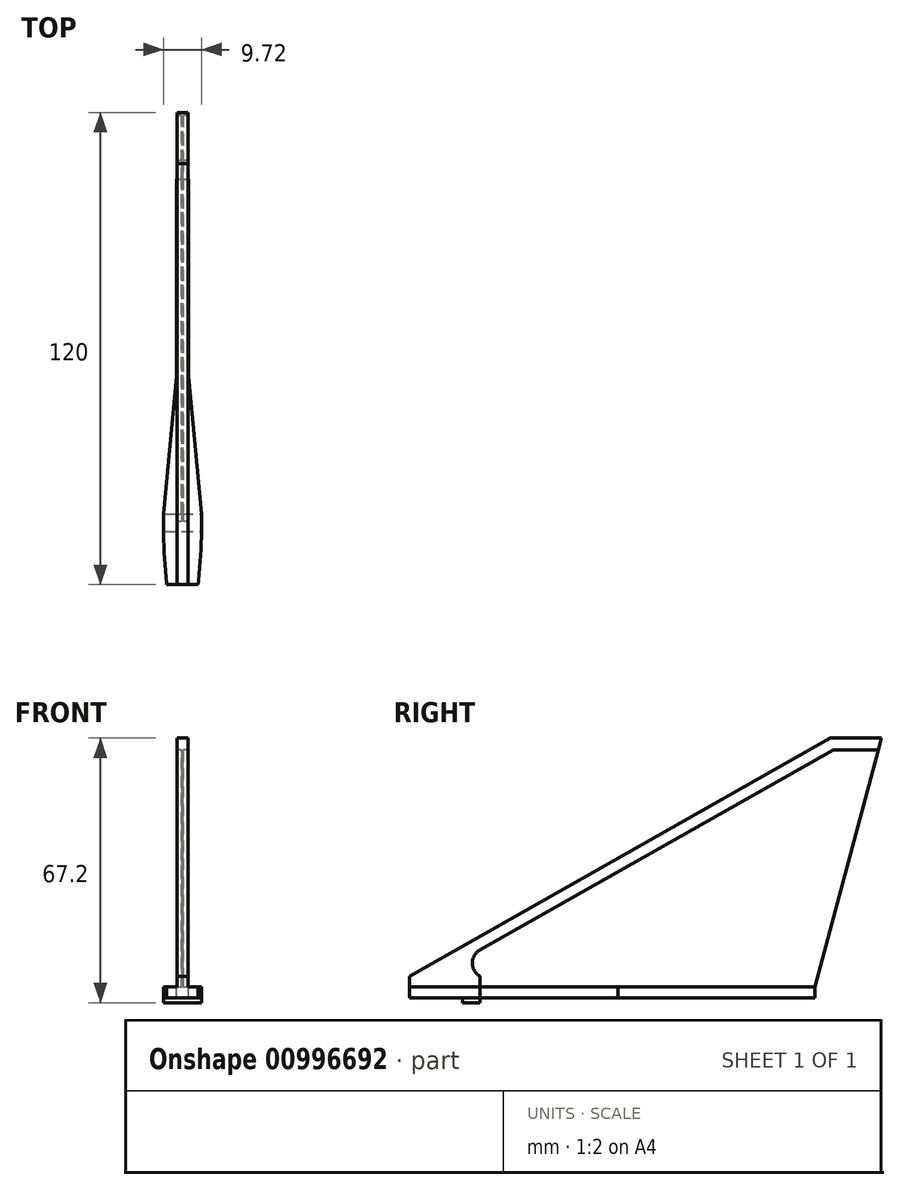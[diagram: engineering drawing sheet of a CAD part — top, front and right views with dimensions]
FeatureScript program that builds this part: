
annotation { "Feature Type Name" : "Feature", "Feature Type Description" : "" }
export const myFeature = defineFeature(function(context is Context, id is Id, definition is map)
    precondition{}
    {
        {
            var Q0;
            Q0=qCreatedBy(makeId("Front.planeOp"),FACE);
            var sketch = newSketch(context, id + "F0", { "sketchPlane" : qUnion([Q0])});
            skLineSegment(sketch, "E0.bottom", {"start": v(-4, 0) * mm, "end": v(4, 0) * mm});
            skLineSegment(sketch, "E0.top", {"start": v(-4, 2.8) * mm, "end": v(-1.4, 2.8) * mm});
            skLineSegment(sketch, "E0.left", {"start": v(-4, 0) * mm, "end": v(-4, 2.8) * mm});
            skLineSegment(sketch, "E0.right", {"start": v(4, 0) * mm, "end": v(4, 2.8) * mm});
            skLineSegment(sketch, "E1.top", {"start": v(-1.4, 5.5) * mm, "end": v(1.4, 5.5) * mm});
            skLineSegment(sketch, "E1.left", {"start": v(-1.4, 2.8) * mm, "end": v(-1.4, 5.5) * mm});
            skLineSegment(sketch, "E1.right", {"start": v(1.4, 2.8) * mm, "end": v(1.4, 5.5) * mm});
            skLineSegment(sketch, "E2", {"start": v(0, -1.58) * mm, "end": v(0, 6.32) * mm, "construction": true});
            skLineSegment(sketch, "E3.trimOffspring", {"start": v(1.4, 2.8) * mm, "end": v(4, 2.8) * mm});
            skSolve(sketch);
        }
        {
            var Q0;
            Q0=qCreatedBy(makeId("Front.planeOp"),FACE);
            cPlane(context, id + "F1", {"entities" : qUnion([Q0]), "cplaneType" : CPlaneType.OFFSET, "offset" : 13.5 * mm, "oppositeDirection" : true, "width" : 150 * mm, "height" : 150 * mm});
        }
        {
            var Q0;
            Q0=qCreatedBy(id+"F1.planeOp",FACE);
            var sketch = newSketch(context, id + "F2", { "sketchPlane" : qUnion([Q0])});
            skLineSegment(sketch, "E4.bottom", {"start": v(-4.85, 0) * mm, "end": v(4.85, 0) * mm});
            skLineSegment(sketch, "E4.top", {"start": v(-4.85, 2.8) * mm, "end": v(-1.4, 2.8) * mm});
            skLineSegment(sketch, "E4.left", {"start": v(-4.85, 0) * mm, "end": v(-4.85, 2.8) * mm});
            skLineSegment(sketch, "E4.right", {"start": v(4.85, 0) * mm, "end": v(4.85, 2.8) * mm});
            skLineSegment(sketch, "E5.top", {"start": v(-1.4, 5.5) * mm, "end": v(1.4, 5.5) * mm});
            skLineSegment(sketch, "E5.left", {"start": v(-1.4, 2.8) * mm, "end": v(-1.4, 5.5) * mm});
            skLineSegment(sketch, "E5.right", {"start": v(1.4, 2.8) * mm, "end": v(1.4, 5.5) * mm});
            skLineSegment(sketch, "E6", {"start": v(0, -4.65) * mm, "end": v(0, 9.3) * mm, "construction": true});
            skLineSegment(sketch, "E7.trimOffspring", {"start": v(1.4, 2.8) * mm, "end": v(4.85, 2.8) * mm});
            skPoint(sketch, "E8.0", {"position": v(0, 0) * mm});
            skSolve(sketch);
        }
        {
            var Q0;
            Q0=qCreatedBy(id+"F1.planeOp",FACE);
            cPlane(context, id + "F3", {"entities" : qUnion([Q0]), "cplaneType" : CPlaneType.OFFSET, "offset" : 4.5 * mm, "oppositeDirection" : true, "width" : 150 * mm, "height" : 150 * mm});
        }
        {
            var Q0;
            Q0=qCreatedBy(id+"F3.planeOp",FACE);
            var sketch = newSketch(context, id + "F4", { "sketchPlane" : qUnion([Q0])});
            skLineSegment(sketch, "E9.0", {"start": v(-1.4, 2.8) * mm, "end": v(-1.4, 5.5) * mm});
            skLineSegment(sketch, "E9.1", {"start": v(-1.4, 5.5) * mm, "end": v(1.4, 5.5) * mm});
            skLineSegment(sketch, "E9.2", {"start": v(4.85, 0) * mm, "end": v(4.85, 2.8) * mm});
            skLineSegment(sketch, "E9.3", {"start": v(-4.85, 0) * mm, "end": v(-4.85, 2.8) * mm});
            skLineSegment(sketch, "E9.4", {"start": v(1.4, 2.8) * mm, "end": v(4.85, 2.8) * mm});
            skLineSegment(sketch, "E9.5", {"start": v(0, -4.65) * mm, "end": v(0, 9.3) * mm, "construction": true});
            skLineSegment(sketch, "E9.6", {"start": v(-4.85, 2.8) * mm, "end": v(-1.4, 2.8) * mm});
            skLineSegment(sketch, "E9.7", {"start": v(-4.85, 0) * mm, "end": v(4.85, 0) * mm});
            skLineSegment(sketch, "E9.8", {"start": v(1.4, 2.8) * mm, "end": v(1.4, 5.5) * mm});
            skSolve(sketch);
        }
        {
            var Q0;
            Q0=qCreatedBy(id+"F3.planeOp",FACE);
            var sketch = newSketch(context, id + "F5", { "sketchPlane" : qUnion([Q0])});
            skLineSegment(sketch, "E10.0", {"start": v(-4.85, 0) * mm, "end": v(-4.85, 2.8) * mm});
            skLineSegment(sketch, "E11.0", {"start": v(-4.85, 0) * mm, "end": v(4.85, 0) * mm});
            skLineSegment(sketch, "E12.0", {"start": v(4.85, 0) * mm, "end": v(4.85, 2.8) * mm});
            skLineSegment(sketch, "E13.0", {"start": v(0, -4.65) * mm, "end": v(0, 9.3) * mm, "construction": true});
            skLineSegment(sketch, "E14", {"start": v(-4.85, 2.8) * mm, "end": v(4.85, 2.8) * mm});
            skSolve(sketch);
        }
        {
            var Q0;
            Q0=qCreatedBy(id+"F3.planeOp",FACE);
            cPlane(context, id + "F6", {"entities" : qUnion([Q0]), "cplaneType" : CPlaneType.OFFSET, "offset" : 35 * mm, "oppositeDirection" : true, "width" : 150 * mm, "height" : 150 * mm});
        }
        {
            var Q0;
            Q0=qCreatedBy(id+"F6.planeOp",FACE);
            var sketch = newSketch(context, id + "F7", { "sketchPlane" : qUnion([Q0])});
            skPoint(sketch, "E15.0", {"position": v(0, 0) * mm});
            skLineSegment(sketch, "E16.bottom", {"start": v(-1.5, 0) * mm, "end": v(1.5, 0) * mm});
            skLineSegment(sketch, "E16.left", {"start": v(-1.5, 0) * mm, "end": v(-1.5, 2.8) * mm});
            skLineSegment(sketch, "E16.right", {"start": v(1.5, 0) * mm, "end": v(1.5, 2.8) * mm});
            skLineSegment(sketch, "E17", {"start": v(0, -1.58) * mm, "end": v(0, 6.32) * mm, "construction": true});
            skLineSegment(sketch, "E18", {"start": v(-1.5, 2.8) * mm, "end": v(1.5, 2.8) * mm});
            skSolve(sketch);
        }
        {
            var Q0;
            Q0=makeQuery(id+"F0.imprint","IMPRINT",FACE,{"disambiguationData":[TD([[makeQuery(id+"F0.imprint","IMPRINT",EDGE,{"derivedFrom":sQuery(id+"F0.wireOp",EDGE,"E0.bottom")}),1.0]])]});
            var Q1;
            Q1=makeQuery(id+"F2.imprint","IMPRINT",FACE,{"disambiguationData":[TD([[makeQuery(id+"F2.imprint","IMPRINT",EDGE,{"derivedFrom":sQuery(id+"F2.wireOp",EDGE,"E4.bottom")}),1.0]])]});
            var Q2;
            Q2=makeQuery(id+"F4.imprint","IMPRINT",FACE,{"disambiguationData":[TD([[makeQuery(id+"F4.imprint","IMPRINT",EDGE,{"derivedFrom":sQuery(id+"F4.wireOp",EDGE,"E9.0")}),-1.0]])]});
            loft(context, id + "F8", {"sheetProfilesArray" : [{ "sheetProfileEntities" : qUnion([Q0]) }, { "sheetProfileEntities" : qUnion([Q1]) }, { "sheetProfileEntities" : qUnion([Q2]) }]});
        }
        {
            var Q1;
            Q1 = qSketchRegion(id + "F5", true);
            var Q2;
            Q2 = qSketchRegion(id + "F7", true);
            loft(context, id + "F9", {"operationType" : NewBodyOperationType.ADD, "sheetProfilesArray" : [{ "sheetProfileEntities" : qUnion([Q1]) }, { "sheetProfileEntities" : qUnion([Q2]) }]});
        }
        {
            var Q0;
            Q0 = qSketchRegion(id + "F7", true);
            extrude(context, id + "F10", {"entities" : qUnion([Q0]), "operationType" : NewBodyOperationType.ADD, "oppositeDirection" : true, "depth" : 50 * mm, "offsetDistance" : 25 * mm});
        }
        {
            var Q0;
            {var subQ0=sQuery(id+"F7.wireOp",EDGE,"E16.bottom");Q0=makeQuery(id+"F10.boolean.opBoolean","MERGE",FACE,{"derivedFrom":[makeQuery(id+"F9.boolean.opBoolean","MERGE",FACE,{"derivedFrom":[makeQuery(id+"F8.opLoft","SWEPT_FACE",FACE,{"disambiguationData":[OSD([sQuery(id+"F0.wireOp",EDGE,"E0.bottom"),sQuery(id+"F0.wireOp",EDGE,"E0.left"),sQuery(id+"F0.wireOp",EDGE,"E0.right"),sQuery(id+"F2.wireOp",EDGE,"E4.bottom"),sQuery(id+"F2.wireOp",EDGE,"E4.left"),sQuery(id+"F2.wireOp",EDGE,"E4.right"),sQuery(id+"F4.wireOp",EDGE,"E9.2"),sQuery(id+"F4.wireOp",EDGE,"E9.3"),sQuery(id+"F4.wireOp",EDGE,"E9.7")])]}),makeQuery(id+"F9.opLoft","SWEPT_FACE",FACE,{"disambiguationData":[OSD([sQuery(id+"F5.wireOp",EDGE,"E10.0"),sQuery(id+"F5.wireOp",EDGE,"E11.0"),sQuery(id+"F5.wireOp",EDGE,"E12.0"),subQ0,sQuery(id+"F7.wireOp",EDGE,"E16.left"),sQuery(id+"F7.wireOp",EDGE,"E16.right")])]})]}),makeQuery(id+"F10.opExtrude","SWEPT_FACE",FACE,{"disambiguationData":[OSD([subQ0])]})]});}
            var sketch = newSketch(context, id + "F11", { "sketchPlane" : qUnion([Q0])});
            skFitSpline(sketch, "E19.0", {"points": [v(-4, 0) * mm, v(-4.39, -4.5) * mm, v(-4.9, -10.5) * mm, v(-4.86, -16.5) * mm, v(-4.85, -18) * mm], "construction": true});
            skFitSpline(sketch, "E20.0", {"points": [v(4, 0) * mm, v(4.39, -4.5) * mm, v(4.9, -10.5) * mm, v(4.86, -16.5) * mm, v(4.85, -18) * mm], "construction": true});
            skPoint(sketch, "E21.0", {"position": v(-4.85, -18) * mm});
            skLineSegment(sketch, "E22", {"start": v(-4.85, -13.5) * mm, "end": v(4.85, -13.5) * mm});
            skLineSegment(sketch, "E23", {"start": v(-4.85, -18) * mm, "end": v(4.85, -18) * mm});
            skLineSegment(sketch, "E24", {"start": v(-4.85, -13.5) * mm, "end": v(-4.85, -18) * mm});
            skLineSegment(sketch, "E25", {"start": v(4.85, -18) * mm, "end": v(4.85, -13.5) * mm});
            skSolve(sketch);
        }
        {
            var Q0;
            Q0 = qSketchRegion(id + "F11", true);
            extrude(context, id + "F12", {"entities" : qUnion([Q0]), "operationType" : NewBodyOperationType.ADD, "depth" : 1.2 * mm, "offsetDistance" : 25 * mm});
        }
        {
            var Q0;
            Q0=qCreatedBy(makeId("Right.planeOp"),FACE);
            var sketch = newSketch(context, id + "F13", { "sketchPlane" : qUnion([Q0])});
            skLineSegment(sketch, "E26", {"start": v(103, 2.8) * mm, "end": v(18, 2.8) * mm, "construction": true});
            skLineSegment(sketch, "E27", {"start": v(103, 2.8) * mm, "end": v(103, 0) * mm, "construction": true});
            skLineSegment(sketch, "E28", {"start": v(18, 0) * mm, "end": v(103, 0) * mm, "construction": true});
            skLineSegment(sketch, "E29", {"start": v(0, 0) * mm, "end": v(13.5, 0) * mm, "construction": true});
            skLineSegment(sketch, "E30", {"start": v(0, 5.5) * mm, "end": v(0, 0) * mm, "construction": true});
            skLineSegment(sketch, "E31", {"start": v(18, 5.5) * mm, "end": v(0, 5.5) * mm, "construction": true});
            skLineSegment(sketch, "E32", {"start": v(18, 5.5) * mm, "end": v(18, 2.8) * mm, "construction": true});
            skLineSegment(sketch, "E33", {"start": v(18, 0) * mm, "end": v(18, -1.2) * mm, "construction": true});
            skLineSegment(sketch, "E34", {"start": v(13.5, -1.2) * mm, "end": v(18, -1.2) * mm, "construction": true});
            skLineSegment(sketch, "E35", {"start": v(13.5, 0) * mm, "end": v(13.5, -1.2) * mm, "construction": true});
            skPoint(sketch, "E36", {"position": v(120, 66) * mm});
            skLineSegment(sketch, "E37", {"start": v(103, 2.8) * mm, "end": v(120, 66) * mm});
            skLineSegment(sketch, "E38", {"start": v(120, 66) * mm, "end": v(107, 66) * mm});
            skLineSegment(sketch, "E39", {"start": v(107, 66) * mm, "end": v(0, 5.5) * mm});
            skLineSegment(sketch, "E40", {"start": v(0, 5.5) * mm, "end": v(18, 5.5) * mm});
            skLineSegment(sketch, "E41", {"start": v(18, 5.5) * mm, "end": v(18, 2.8) * mm});
            skLineSegment(sketch, "E42", {"start": v(18, 2.8) * mm, "end": v(103, 2.8) * mm});
            skLineSegment(sketch, "E43.0", {"start": v(107.79, 63) * mm, "end": v(18, 12.23) * mm});
            skLineSegment(sketch, "E43.1", {"start": v(119.2, 63) * mm, "end": v(107.79, 63) * mm});
            skArc(sketch, "E44", {"start": v(18, 12.23) * mm, "mid": v(16.04, 8.87) * mm, "end": v(18, 5.5) * mm});
            skSolve(sketch);
        }
        {
            var Q0;
            Q0=makeQuery(id+"F13.imprint","IMPRINT",FACE,{"disambiguationData":[TD([[makeQuery(id+"F13.imprint","IMPRINT",EDGE,{"derivedFrom":sQuery(id+"F13.wireOp",EDGE,"E41")}),1.0]])]});
            extrude(context, id + "F14", {"entities" : qUnion([Q0]), "operationType" : NewBodyOperationType.ADD, "endBound" : BoundingType.SYMMETRIC, "depth" : 0.4 * mm, "offsetDistance" : 25 * mm});
        }
        {
            var Q0;
            {var subQ0=sQuery(id+"F13.wireOp",EDGE,"E38");Q0=makeQuery(id+"F13.imprint","IMPRINT",FACE,{"disambiguationData":[TD([[makeQuery(id+"F13.imprint","IMPRINT",EDGE,{"derivedFrom":subQ0}),1.0]])]});}
            extrude(context, id + "F15", {"entities" : qUnion([Q0]), "operationType" : NewBodyOperationType.ADD, "endBound" : BoundingType.SYMMETRIC, "depth" : 2.8 * mm, "offsetDistance" : 25 * mm});
        }
    });
